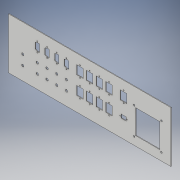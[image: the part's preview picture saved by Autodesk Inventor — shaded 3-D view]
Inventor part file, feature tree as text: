
AUTODESK INVENTOR PART (.ipt)
format: ipt  version: 2017 (Build 210142000, 142)  size: 418,304 bytes
history: native  units: in
note: dims shown in document units (in); Inventor stores cm internally (conversion verified against a paired STEP export)
features: extrude x6, other x4, hole x4, sketch x3, projected_geometry x1
ambient origin geometry x8: Origin, YZ Plane, XZ Plane, XY Plane, X Axis, Y Axis, Z Axis, Center Point
bodies: Solid1 (feature_tree)
feature tree (18):
  extrude  "pdu"  Depth=5.256in
  other  "dsub9 sketch"
  other  "CAT7 sketch"
  hole  "airflow holes"  [1 undecoded]
  extrude  "airflow cutout"  Depth=1.0in
  hole  "CAT7 holes"  [1 undecoded]
  extrude  "CAT7 cutout"  Depth=1.0in
  extrude  "sma cutouts"  Depth=1.0in
  other  "sc/sc"
  hole  "sc/sc holes"  [1 undecoded]
  extrude  "sc cutout"  Depth=1.0in
  extrude  "Extrusion12"  Depth=1.0in
  hole  "Hole6"  [1 undecoded]
  sketch  "Sketch1"  dims[d0=16.73in d1=5.256in]
  sketch  "Sketch5"  dims[d2=0.065in d3=0.0in d4=0.089in]
  sketch  "Sketch7"  dims[d5=0.089in d6=0.984in d7=0.166in d8=0.166in d9=0.166in d10=0.166in d11=0.525in d12=0.65in d13=0.325in d14=0.325in d15=0.12in d16=0.12in d17=2.97in d18=0.23in d19=0.46in d21=0.2952in d22=1.5748in d24=1.5in d25=0.3937in d27=1.0in d47=0.9in d48=0.675in d49=0.089in d50=0.089in d51=1.142in d52=3.216in d53=7.359in d54=0.7874in d56=1.852in d57=0.3937in d59=1.0in d63=3.3in d64=3.3in d65=12.7in d66=0.535in d67=2.5in d68=2.5in d69=2.81in d70=0.177in d71=0.177in d72=0.177in d73=0.177in d76=0.177in d77=0.75in d78=0.332in d79=0.25in d80=0.5635in d81=1.0in d82=0.8108in d83=3.3in d84=3.3in d85=12.7in d86=0.535in d87=2.5in d88=2.5in d89=2.81in d90=0.177in d91=0.177in d92=0.177in d93=0.177in d94=0.0in d95=0.0in d105=0.116in d106=0.224in d107=0.375in d108=0.25in d109=0.5635in d110=0.349in d111=0.8108in d112=0.0in d113=0.0in d123=0.25in d124=0.235in d128=0.0in d129=0.0in d130=1.5748in d132=1.0in d133=0.3937in d135=1.0in d138=1.5748in d140=0.3937in d143=1.5748in d145=0.3937in d146=0.9in d147=0.675in d148=0.089in d149=0.089in d150=1.142in d151=1.5in d152=1.019in d153=0.53in d154=0.37in d155=0.7087in d156=0.094in d157=0.75in d158=0.173in d159=0.25in d160=90.0deg d161=1.0in d162=0.8108in d163=1.0in d164=0.0in d165=1.469in d173=1.5748in d175=1.0in d176=0.3937in d178=1.0in d180=1.0in d181=0.0in d182=0.116in d183=0.75in d184=0.225in d185=0.25in d186=0.5635in d187=1.0in d188=0.8108in d189=0.7874in d191=1.5in d192=0.3937in d194=1.0in d196=0.7874in d198=1.0in d199=0.3937in d201=1.0in d203=1.5748in d205=1.0in d206=0.3937in d208=1.0in d96=1.0in d97=1.0in]
  other  "sma"
  projected_geometry  "Projected Loop1"
note: 4 required parameter values undecoded (feature->parameter linkage not recoverable at this tier; creation-order binding heuristic only, values carry confidence <= 0.55)
